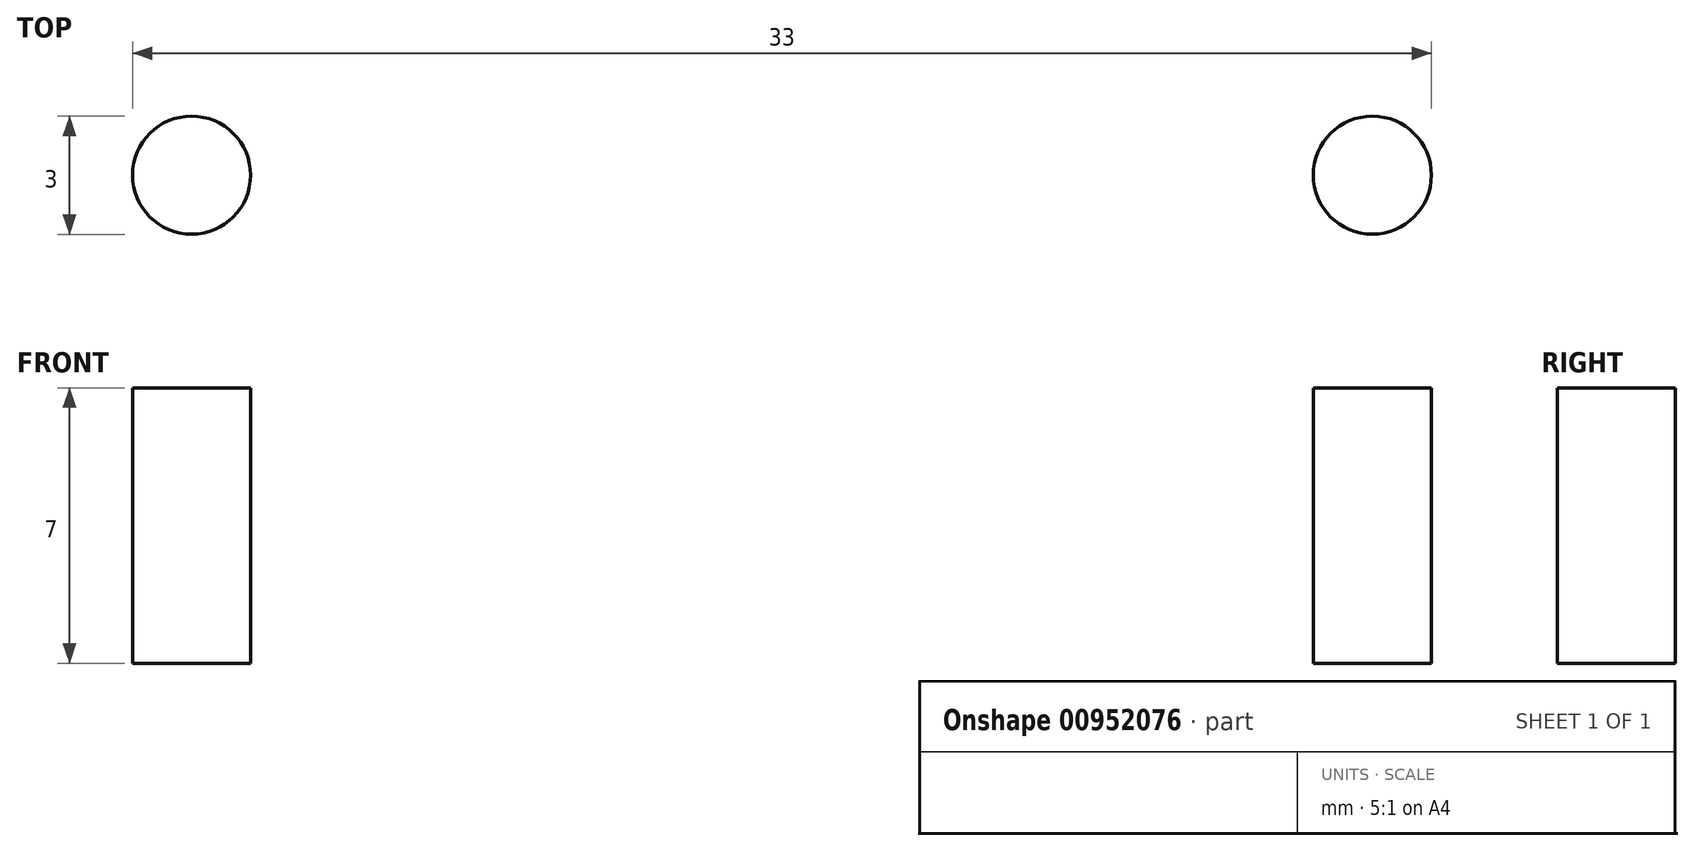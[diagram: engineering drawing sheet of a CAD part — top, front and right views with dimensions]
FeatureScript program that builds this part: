
annotation { "Feature Type Name" : "Feature", "Feature Type Description" : "" }
export const myFeature = defineFeature(function(context is Context, id is Id, definition is map)
    precondition{}
    {
        {
            var Q0;
            Q0=qCreatedBy(makeId("Top.planeOp"),FACE);
            var sketch = newSketch(context, id + "F0", { "sketchPlane" : qUnion([Q0])});
            skCircle(sketch, "E0", {"center": v(-15, 3.45) * mm, "radius": 1.5 * mm});
            skCircle(sketch, "E1.MirrorC", {"center": v(15, 3.45) * mm, "radius": 1.5 * mm});
            skSolve(sketch);
        }
        {
            var Q0;
            Q0 = qSketchRegion(id + "F0", true);
            extrude(context, id + "F1", {"entities" : qUnion([Q0]), "depth" : 7 * mm, "offsetDistance" : 25 * mm});
        }
    });
